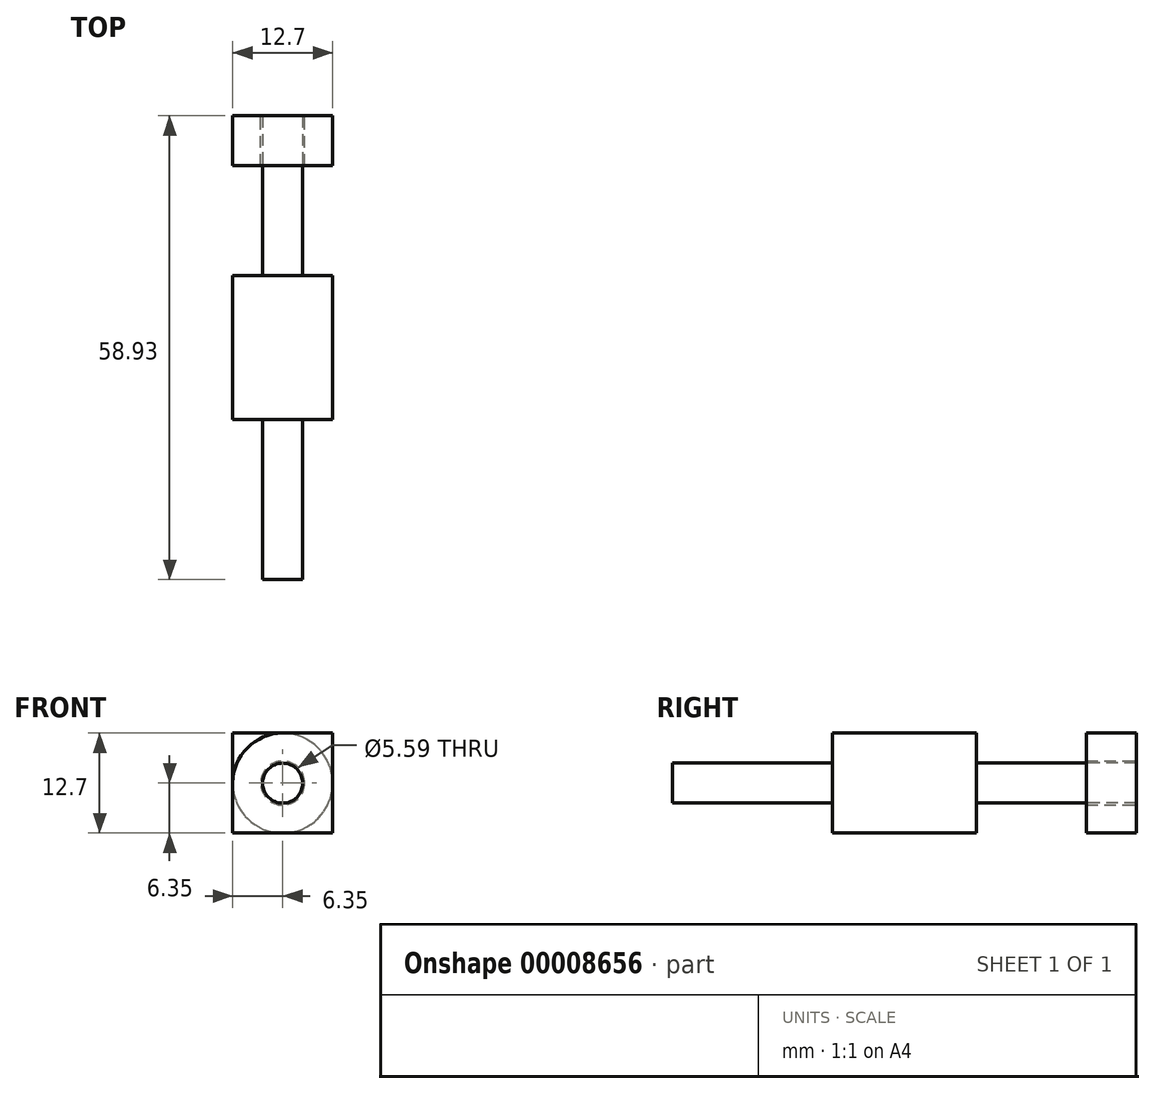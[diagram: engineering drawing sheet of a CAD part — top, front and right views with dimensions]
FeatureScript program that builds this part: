
annotation { "Feature Type Name" : "Feature", "Feature Type Description" : "" }
export const myFeature = defineFeature(function(context is Context, id is Id, definition is map)
    precondition{}
    {
        {
            var Q0;
            Q0=qCreatedBy(makeId("Front.planeOp"),FACE);
            var sketch = newSketch(context, id + "F0", { "sketchPlane" : qUnion([Q0])});
            skLineSegment(sketch, "E0.bottom", {"start": v(-6.35, 6.35) * mm, "end": v(6.35, 6.35) * mm});
            skLineSegment(sketch, "E0.top", {"start": v(-6.35, -6.35) * mm, "end": v(6.35, -6.35) * mm});
            skLineSegment(sketch, "E0.left", {"start": v(-6.35, 6.35) * mm, "end": v(-6.35, -6.35) * mm});
            skLineSegment(sketch, "E0.right", {"start": v(6.35, 6.35) * mm, "end": v(6.35, -6.35) * mm});
            skSolve(sketch);
        }
        {
            var Q0;
            Q0 = qSketchRegion(id + "F0", true);
            extrude(context, id + "F1", {"entities" : qUnion([Q0]), "depth" : 18.29 * mm});
        }
        {
            var Q0;
            Q0=makeQuery(id+"F1.opExtrude","CAP_FACE",FACE,{"disambiguationData":[OSD([sQuery(id+"F0.wireOp",EDGE,"E0.bottom"),sQuery(id+"F0.wireOp",EDGE,"E0.top"),sQuery(id+"F0.wireOp",EDGE,"E0.left"),sQuery(id+"F0.wireOp",EDGE,"E0.right")])],"isStart":true});
            var sketch = newSketch(context, id + "F2", { "sketchPlane" : qUnion([Q0])});
            skCircle(sketch, "E1", {"center": v(0, 0) * mm, "radius": 2.54 * mm});
            skSolve(sketch);
        }
        {
            var Q0;
            Q0 = qSketchRegion(id + "F2", true);
            extrude(context, id + "F3", {"entities" : qUnion([Q0]), "operationType" : NewBodyOperationType.ADD, "depth" : 20.32 * mm});
        }
        {
            var Q0;
            Q0=makeQuery(id+"F1.opExtrude","CAP_FACE",FACE,{"disambiguationData":[OSD([sQuery(id+"F0.wireOp",EDGE,"E0.bottom"),sQuery(id+"F0.wireOp",EDGE,"E0.top"),sQuery(id+"F0.wireOp",EDGE,"E0.left"),sQuery(id+"F0.wireOp",EDGE,"E0.right")])],"isStart":false});
            var sketch = newSketch(context, id + "F4", { "sketchPlane" : qUnion([Q0])});
            skCircle(sketch, "E2", {"center": v(0, 0) * mm, "radius": 2.54 * mm});
            skSolve(sketch);
        }
        {
            var Q0;
            Q0 = qSketchRegion(id + "F4", true);
            extrude(context, id + "F5", {"entities" : qUnion([Q0]), "operationType" : NewBodyOperationType.ADD, "depth" : 20.32 * mm});
        }
        {
            var Q0;
            Q0=makeQuery(id+"F3.opExtrude","CAP_FACE",FACE,{"disambiguationData":[OSD([sQuery(id+"F2.wireOp",EDGE,"E1")])],"isStart":false});
            var sketch = newSketch(context, id + "F6", { "sketchPlane" : qUnion([Q0])});
            skCircle(sketch, "E3", {"center": v(0, 0) * mm, "radius": 6.35 * mm});
            skCircle(sketch, "E4", {"center": v(0, 0) * mm, "radius": 2.8 * mm});
            skSolve(sketch);
        }
        {
            var Q0;
            Q0 = qSketchRegion(id + "F6", true);
            extrude(context, id + "F7", {"entities" : qUnion([Q0]), "oppositeDirection" : true, "depth" : 6.35 * mm});
        }
    });
